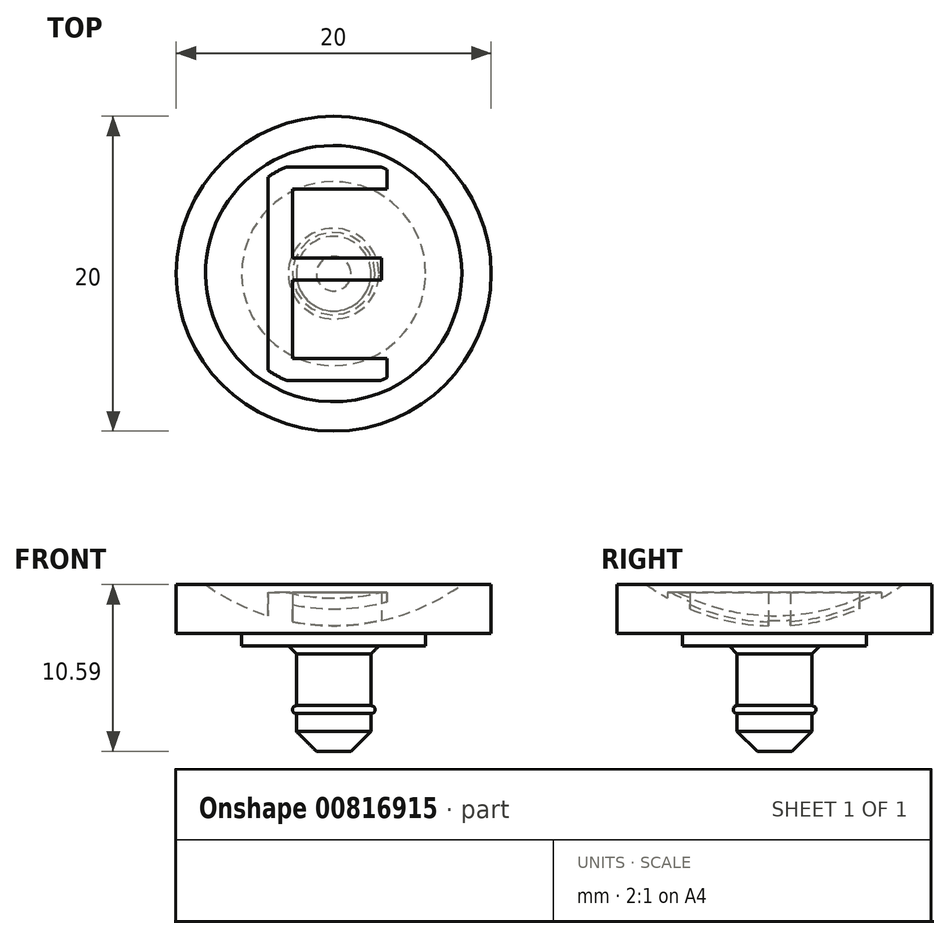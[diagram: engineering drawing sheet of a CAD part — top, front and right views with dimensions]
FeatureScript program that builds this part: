
annotation { "Feature Type Name" : "Feature", "Feature Type Description" : "" }
export const myFeature = defineFeature(function(context is Context, id is Id, definition is map)
    precondition{}
    {
        {
            var Q0;
            Q0=qCreatedBy(makeId("Front.planeOp"),FACE);
            var sketch = newSketch(context, id + "F0", { "sketchPlane" : qUnion([Q0])});
            skLineSegment(sketch, "E0", {"start": v(4.22, 0) * mm, "end": v(10, 0) * mm});
            skLineSegment(sketch, "E1", {"start": v(10, 0) * mm, "end": v(10, 5.48) * mm});
            skArc(sketch, "E2", {"start": v(0, 1.27) * mm, "mid": v(5.43, 2.37) * mm, "end": v(10, 5.48) * mm});
            skLineSegment(sketch, "E3", {"start": v(0, 1.27) * mm, "end": v(0, 0) * mm});
            skLineSegment(sketch, "E4", {"start": v(2.37, 0) * mm, "end": v(2.68, 0) * mm});
            skLineSegment(sketch, "E5", {"start": v(2.37, 0) * mm, "end": v(2.37, -3.8) * mm});
            skLineSegment(sketch, "E6", {"start": v(2.37, -6.7) * mm, "end": v(0, -6.7) * mm});
            skLineSegment(sketch, "E7", {"start": v(0, -6.7) * mm, "end": v(0, 0) * mm});
            skArc(sketch, "E8", {"start": v(2.37, -4.3) * mm, "mid": v(2.63, -4.05) * mm, "end": v(2.37, -3.8) * mm});
            skLineSegment(sketch, "E9.trimOffspring", {"start": v(2.37, -4.3) * mm, "end": v(2.37, -6.7) * mm});
            skLineSegment(sketch, "E10", {"start": v(2.68, 0) * mm, "end": v(4.22, 0) * mm});
            skSolve(sketch);
        }
        {
            var Q0;
            Q0=qSketchRegion(id+"F0",true);
            var Q1;
            Q1=sQuery(id+"F0.wireOp",EDGE,"E3");
            revolve(context, id + "F1", {"surfaceOperationType" : NewSurfaceOperationType.NEW, "entities" : qUnion([Q0]), "axis" : qUnion([Q1]), "revolveType" : RevolveType.FULL});
        }
        {
            var Q0;
            Q0=qCreatedBy(makeId("Top.planeOp"),FACE);
            var sketch = newSketch(context, id + "F2", { "sketchPlane" : qUnion([Q0])});
            skText(sketch, "E11", { "text": "E", "fontName": "OpenSans-Regular.ttf"});
            const initialGuessF2  = {"E11": [-0.00605, -0.0068, 1, 0, 0.0137]};
            skSetInitialGuess(sketch, initialGuessF2);
            skSolve(sketch);
        }
        {
            var Q0;
            Q0=qSketchRegion(id+"F2",true);
            extrude(context, id + "F3", {"entities" : qUnion([Q0]), "operationType" : NewBodyOperationType.ADD, "depth" : 3.4 * mm, "offsetDistance" : 25.4 * mm});
        }
        {
            var Q0;
            Q0=qCreatedBy(makeId("Right.planeOp"),FACE);
            var sketch = newSketch(context, id + "F4", { "sketchPlane" : qUnion([Q0])});
            skLineSegment(sketch, "E12.bottom", {"start": v(-221.51, 121.22) * mm, "end": v(217.82, 121.22) * mm});
            skLineSegment(sketch, "E12.top", {"start": v(-221.51, 3.89) * mm, "end": v(217.82, 3.89) * mm});
            skLineSegment(sketch, "E12.left", {"start": v(-221.51, 121.22) * mm, "end": v(-221.51, 3.89) * mm});
            skLineSegment(sketch, "E12.right", {"start": v(217.82, 121.22) * mm, "end": v(217.82, 3.89) * mm});
            skSolve(sketch);
        }
        {
            var Q0;
            Q0=qSketchRegion(id+"F4",true);
            extrude(context, id + "F5", {"entities" : qUnion([Q0]), "operationType" : NewBodyOperationType.REMOVE, "endBound" : BoundingType.SYMMETRIC, "depth" : 25.4 * mm, "offsetDistance" : 25.4 * mm});
        }
        {
            var Q0;
            Q0=makeQuery(id+"F1.opRevolve","SWEPT_EDGE",EDGE,{"disambiguationData":[OSD([sQuery(id+"F0.wireOp",EDGE,"E6"),sQuery(id+"F0.wireOp",EDGE,"E9.trimOffspring")])]});
            chamfer(context, id + "F6", {"entities" : qUnion([Q0]), "width" : 1.27 * mm, "tangentPropagation" : true});
        }
        {
            var Q0;
            Q0=makeQuery(id+"F1.opRevolve","SWEPT_FACE",FACE,{"disambiguationData":[OSD([sQuery(id+"F0.wireOp",EDGE,"E0"),sQuery(id+"F0.wireOp",EDGE,"E4"),sQuery(id+"F0.wireOp",EDGE,"E10")])]});
            var sketch = newSketch(context, id + "F7", { "sketchPlane" : qUnion([Q0])});
            skCircle(sketch, "E13", {"center": v(0, 0) * mm, "radius": 5.84 * mm});
            skCircle(sketch, "E14", {"center": v(0, 0) * mm, "radius": 14.28 * mm});
            skSolve(sketch);
        }
        {
            var Q0;
            Q0=makeQuery(id+"F7.imprint","IMPRINT",FACE,{"disambiguationData":[TD([[makeQuery(id+"F7.imprint","IMPRINT",EDGE,{"derivedFrom":sQuery(id+"F7.wireOp",EDGE,"E14")}),1.0]])]});
            var Q1;
            Q1=makeQuery(id+"F7.imprint","IMPRINT",FACE,{"disambiguationData":[TD([[makeQuery(id+"F7.imprint","IMPRINT",EDGE,{"derivedFrom":sQuery(id+"F7.wireOp",EDGE,"E13")}),-1.0]])]});
            extrude(context, id + "F8", {"entities" : qUnion([Q0, Q1]), "operationType" : NewBodyOperationType.REMOVE, "oppositeDirection" : true, "depth" : .8 * mm, "offsetDistance" : 25.4 * mm});
        }
        {
            var Q0;
            Q0=makeQuery(id+"F1.opRevolve","SWEPT_EDGE",EDGE,{"disambiguationData":[OSD([sQuery(id+"F0.wireOp",EDGE,"E4"),sQuery(id+"F0.wireOp",EDGE,"E5")])]});
            chamfer(context, id + "F9", {"entities" : qUnion([Q0]), "width" : 0.5 * mm, "tangentPropagation" : true});
        }
    });
